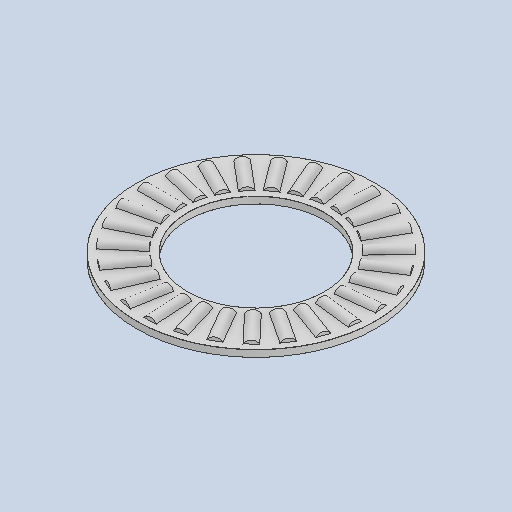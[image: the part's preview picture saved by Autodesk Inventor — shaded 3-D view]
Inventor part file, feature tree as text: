
AUTODESK INVENTOR PART (.ipt)
format: ipt  version: 2023 (Build 270158030, 158C)  size: 373,760 bytes
history: native  units: in
note: dims shown in document units (in); Inventor stores cm internally (conversion verified against a paired STEP export)
features: other x26, revolve x1, pattern_circular x1
ambient origin geometry x8: Origin, YZ Plane, XZ Plane, XY Plane, X Axis, Y Axis, Z Axis, Center Point
bodies: Solid1 (feature_tree), Solid2 (feature_tree), Solid3 (feature_tree), Solid4 (feature_tree), Solid5 (feature_tree), Solid6 (feature_tree), Solid7 (feature_tree), Solid8 (feature_tree), Solid9 (feature_tree), Solid10 (feature_tree), Solid11 (feature_tree), Solid12 (feature_tree), Solid13 (feature_tree), Solid14 (feature_tree), Solid15 (feature_tree), Solid16 (feature_tree), Solid17 (feature_tree), Solid18 (feature_tree), Solid19 (feature_tree), Solid20 (feature_tree), Solid21 (feature_tree), Solid22 (feature_tree), Solid23 (feature_tree), Solid24 (feature_tree), Solid25 (feature_tree), Solid26 (feature_tree), Solid27 (feature_tree), Solid28 (feature_tree)
feature tree (28):
  revolve  "Revolve2"  [1 undecoded]
  pattern_circular  "CirPattern2"
  other  "CirPattern3[1]"
  other  "CirPattern3[2]"
  other  "CirPattern3[3]"
  other  "CirPattern3[4]"
  other  "CirPattern3[5]"
  other  "CirPattern3[6]"
  other  "CirPattern3[7]"
  other  "CirPattern3[8]"
  other  "CirPattern3[9]"
  other  "CirPattern3[10]"
  other  "CirPattern3[11]"
  other  "CirPattern3[12]"
  other  "CirPattern3[13]"
  other  "CirPattern3[14]"
  other  "CirPattern3[15]"
  other  "CirPattern3[16]"
  other  "CirPattern3[17]"
  other  "CirPattern3[18]"
  other  "CirPattern3[19]"
  other  "CirPattern3[20]"
  other  "CirPattern3[21]"
  other  "CirPattern3[22]"
  other  "CirPattern3[23]"
  other  "CirPattern3[24]"
  other  "CirPattern3[25]"
  other  "CirPattern3[26]"
note: 1 required parameter value undecoded (feature->parameter linkage not recoverable at this tier; creation-order binding heuristic only, values carry confidence <= 0.55)
